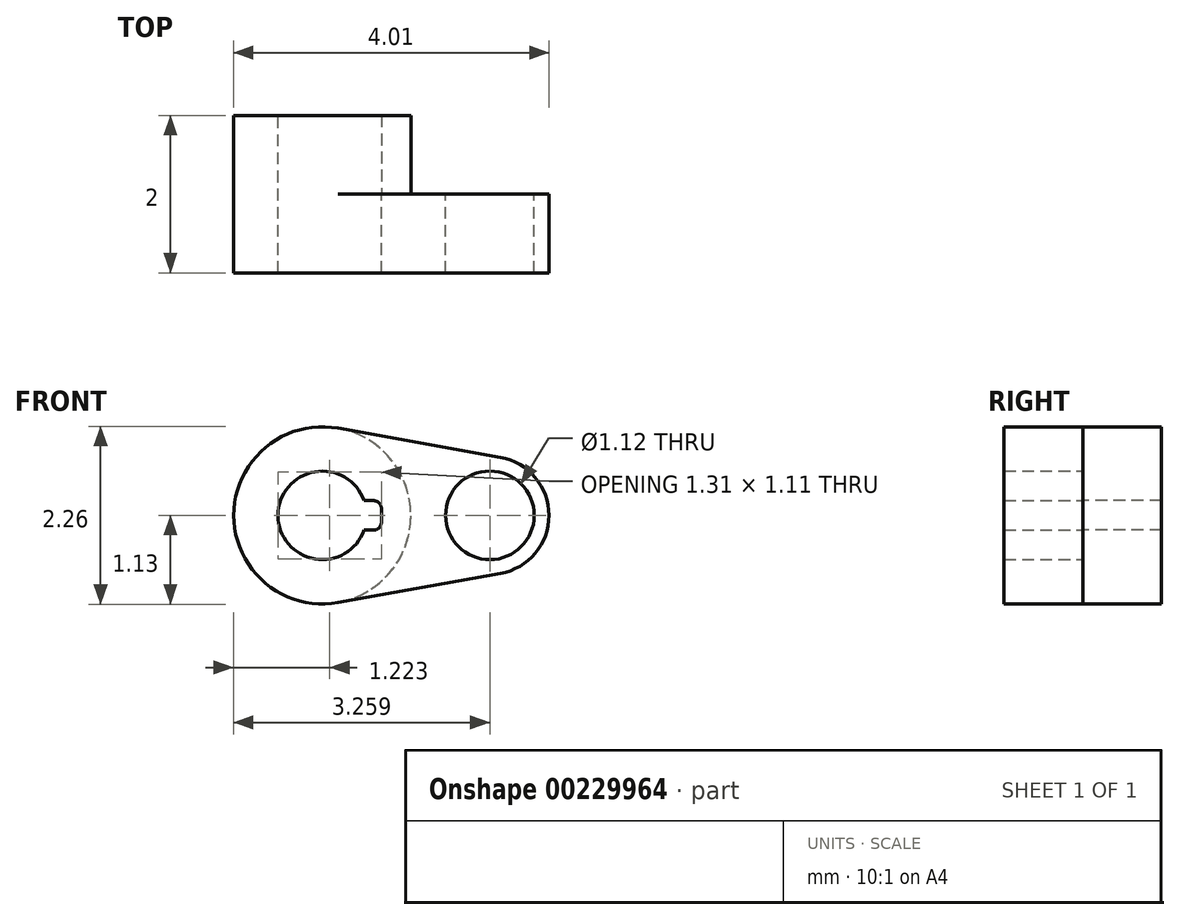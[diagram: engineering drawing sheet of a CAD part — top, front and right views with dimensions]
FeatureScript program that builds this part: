
annotation { "Feature Type Name" : "Feature", "Feature Type Description" : "" }
export const myFeature = defineFeature(function(context is Context, id is Id, definition is map)
    precondition{}
    {
        {
            var Q0;
            Q0=qCreatedBy(makeId("Front.planeOp"),FACE);
            var sketch = newSketch(context, id + "F0", { "sketchPlane" : qUnion([Q0])});
            skCircle(sketch, "E0", {"center": v(-12.04, 0) * mm, "radius": 1.13 * mm});
            skCircle(sketch, "E1", {"center": v(-9.91, 0) * mm, "radius": 0.75 * mm});
            skLineSegment(sketch, "E2", {"start": v(-11.84, 1.1) * mm, "end": v(-9.78, 0.74) * mm});
            skLineSegment(sketch, "E3", {"start": v(-11.84, -1.1) * mm, "end": v(-9.78, -0.74) * mm});
            skCircle(sketch, "E4", {"center": v(-12.04, 0) * mm, "radius": 0.56 * mm});
            skCircle(sketch, "E5", {"center": v(-9.91, 0) * mm, "radius": 0.56 * mm});
            skLineSegment(sketch, "E6.bottom", {"start": v(-11.3, -0.19) * mm, "end": v(-12.8, -0.19) * mm});
            skLineSegment(sketch, "E6.top", {"start": v(-11.3, 0.19) * mm, "end": v(-12.8, 0.19) * mm});
            skLineSegment(sketch, "E6.left", {"start": v(-11.3, -0.19) * mm, "end": v(-11.3, 0.19) * mm});
            skLineSegment(sketch, "E6.right", {"start": v(-12.8, -0.19) * mm, "end": v(-12.8, 0.19) * mm});
            skSolve(sketch);
        }
        {
            var Q0;
            {var subQ0=sQuery(id+"F0.wireOp",EDGE,"E2");Q0=makeQuery(id+"F0.imprint","IMPRINT",FACE,{"disambiguationData":[TD([[makeQuery(id+"F0.imprint","IMPRINT",EDGE,{"derivedFrom":subQ0}),-1.0]])]});}
            var Q1;
            Q1=makeQuery(id+"F0.imprint","IMPRINT",FACE,{"disambiguationData":[TD([[makeQuery(id+"F0.imprint","IMPRINT",EDGE,{"derivedFrom":sQuery(id+"F0.wireOp",EDGE,"E5")}),-1.0]])]});
            var Q2;
            {var subQ11=sQuery(id+"F0.wireOp",EDGE,"E6.left");Q2=makeQuery(id+"F0.imprint","IMPRINT",FACE,{"disambiguationData":[TD([[makeQuery(id+"F0.imprint","IMPRINT",EDGE,{"derivedFrom":subQ11}),-1.0]])]});}
            var Q3;
            {var subQ5=sQuery(id+"F0.wireOp",EDGE,"E6.right");Q3=makeQuery(id+"F0.imprint","IMPRINT",FACE,{"disambiguationData":[TD([[makeQuery(id+"F0.imprint","IMPRINT",EDGE,{"derivedFrom":subQ5}),-1.0]])]});}
            extrude(context, id + "F1", {"entities" : qUnion([Q0, Q1, Q2, Q3]), "depth" : 1 * mm});
        }
        {
            var Q0;
            Q0=makeQuery(id+"F1.opExtrude","SWEPT_EDGE",EDGE,{"disambiguationData":[OSD([sQuery(id+"F0.wireOp",EDGE,"E6.top"),sQuery(id+"F0.wireOp",EDGE,"E6.left")])]});
            var Q1;
            Q1=makeQuery(id+"F1.opExtrude","SWEPT_EDGE",EDGE,{"disambiguationData":[OSD([sQuery(id+"F0.wireOp",EDGE,"E6.bottom"),sQuery(id+"F0.wireOp",EDGE,"E6.left")])]});
            fillet(context, id + "F2", {"entities" : qUnion([Q0, Q1]), "radius" : 0.1 * mm, "tangentPropagation" : true, "allowEdgeOverflow" : false});
        }
        {
            var Q0;
            {var subQ11=sQuery(id+"F0.wireOp",EDGE,"E6.left");Q0=makeQuery(id+"F0.imprint","IMPRINT",FACE,{"disambiguationData":[TD([[makeQuery(id+"F0.imprint","IMPRINT",EDGE,{"derivedFrom":subQ11}),-1.0]])]});}
            var Q1;
            {var subQ5=sQuery(id+"F0.wireOp",EDGE,"E6.right");Q1=makeQuery(id+"F0.imprint","IMPRINT",FACE,{"disambiguationData":[TD([[makeQuery(id+"F0.imprint","IMPRINT",EDGE,{"derivedFrom":subQ5}),-1.0]])]});}
            extrude(context, id + "F3", {"entities" : qUnion([Q0, Q1]), "operationType" : NewBodyOperationType.ADD, "oppositeDirection" : true, "depth" : 1 * mm});
        }
        {
            var Q0;
            Q0=makeQuery(id+"F3.opExtrude","SWEPT_EDGE",EDGE,{"disambiguationData":[OSD([sQuery(id+"F0.wireOp",EDGE,"E6.top"),sQuery(id+"F0.wireOp",EDGE,"E6.left")])]});
            var Q1;
            Q1=makeQuery(id+"F3.opExtrude","SWEPT_EDGE",EDGE,{"disambiguationData":[OSD([sQuery(id+"F0.wireOp",EDGE,"E6.bottom"),sQuery(id+"F0.wireOp",EDGE,"E6.left")])]});
            fillet(context, id + "F4", {"entities" : qUnion([Q0, Q1]), "radius" : 0.1 * mm, "tangentPropagation" : true, "allowEdgeOverflow" : false});
        }
    });
